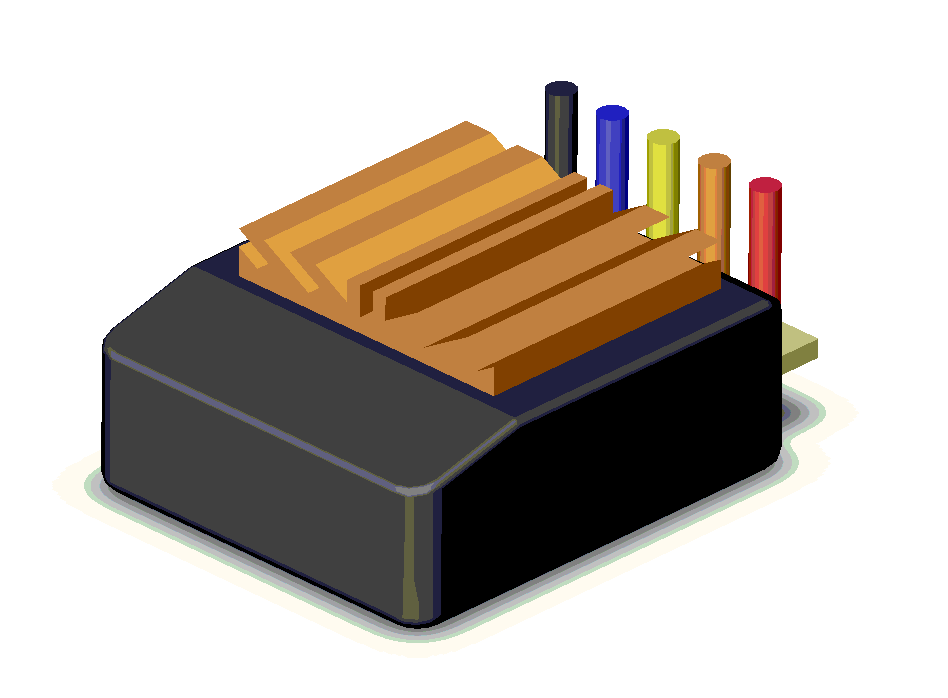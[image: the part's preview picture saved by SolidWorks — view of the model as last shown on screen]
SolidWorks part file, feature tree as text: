
SOLIDWORKS PART (.sldprt)
format: sldprt  version: not decoded by parser v0  size: 235,008 bytes
history: native  units: mm
features: sketch x4, extrude x4, fillet x4, chamfer x2, plane x2 (+8 scaffold rows collapsed)
feature tree (24):
  scaffold x8  (default folders/planes/origin — collapsed)
  sketch  "Sketch1"  dims[D1=30.0mm D2=26.0mm]
  extrude  "Base-Extrude"  Depth=11mm
  chamfer  "Chamfer1"  Distance=8mm
  chamfer  "Chamfer2"  Distance=2mm Angle=30deg
  fillet  "Fillet3"  Radius=2mm
  fillet  "Fillet4"  Radius=1mm
  fillet  "Fillet5"  Radius=1mm
  fillet  "Fillet6"  Radius=0.5mm
  plane  "Plane1"  Offset=3mm
  sketch  "Sketch3"  dims[c1.D1=3.0mm c1.D2=3.0mm c1.D3=3.0mm c1.D4=20.0mm c2.D4=30.0deg c2.D5=~12.769684mm c3.D5=30.0deg c3.D15=8.5mm c3.D16=11.5mm c3.D18=1.0mm c3.D19=~1.845299mm c3.D20=~1.845299mm c3.D3=1.0mm c3.D14=3.0mm c3.D21=~1.690599mm c3.D6=1.0mm c3.D7=1.0mm c3.D8=1.0mm c3.D9=1.0mm c3.D10=1.0mm c3.D11=1.0mm c3.D12=1.0mm c3.D13=1.0mm c4.D14=1.0mm c4.D16=1.0mm c4.D17=1.0mm c4.D18=1.0mm]
  extrude  "Boss-Extrude1"  Depth=18mm
  plane  "Plane2"  Offset=3.5mm
  sketch  "Sketch4"  dims[D1=3.25mm D2=3.25mm D3=5.0mm]
  extrude  "Boss-Extrude2"  Depth=1.2mm
  sketch  "Sketch5"  dims[D1=1.9mm D2=13.0mm D3=2.5mm D4=4.0mm D5=8.0mm D6=4.0mm D7=8.0mm D8=2.5mm D9=2.5mm D10=2.5mm D11=2.5mm]
  extrude  "Boss-Extrude3"  Depth=10mm
decode coverage: 14 of 14 modeling features carry decoded parameters
note: ~ marks probable driven/reference dimensions
note: suppression state not decoded; provenance and decode notes live in map.json
